# Revit family: Haworth_Masters_Desk_DoublePedRectangularTop
name_source: partatom
category: Furniture Systems
revit_build: Autodesk Revit 2018 (Build: 20170223_1515(x64)
units: mm (PartAtom-declared; Revit-internal decimal feet)

## family parameters
Always vertical = Yes
Cut with Voids When Loaded = No
OmniClass Number = 23.40.70.14.64.21
OmniClass Title = Systems Furniture
Part Type = Normal
Room Calculation Point = No
Round Connector Dimension = Use Diameter
Shared = No
Work Plane-Based = No

## types (4) — shared parameters
Actual Depth = 36"
Actual Height = 29 1/8"
Actual Width = 78"
Assembly Code = E2020200
Bar Pull = No
Classic Pull = Yes
Custom Size = No
Depth = 36"
Finger Pull = No
Linear Pull = No
Manufacturer = Haworth
Max. Depth = 36"
Max. Width = 78"
Min. Depth = 30"
Min. Width = 66"
Model = Haworth Masters
Pedestal Depth = 29"
Revision Number = 1
Size = Verify Final Dim. w/ Haworth
Standard Depths = 30, 36 in.
Standard Widths = 66, 72, 78 in.
Sustainability Info = https://www.haworth.com
Thickness = 1 3/16"
URL = www.haworth.com
URL - Product = http://www.haworth.com
Warranty = http://www.haworth.com
Width = 78"

## per-type parameters (varying)
| type | Description | Full Overlay Modesty | Inset Modesty | Void Dimension |
| False Pedestal Modesty - Two Box/Box/File - 36d 78w | Haworth - Masters Desk - Double Ped - Rectangular Top - False Pedestal Modesty - Two Box/Box/File - 36d 78w | No | Yes | 0" |
| False Pedestal Modesty - One Box/Box/File & One File/File - 36d 78w | Haworth - Masters Desk - Double Ped - Rectangular Top - False Pedestal Modesty - One Box/Box/File and One File/File - 36d 78w | No | Yes | 0" |
| Full Overlay Modesty - Two Box/Box/File - 36d 78w | Haworth - Masters Desk - Double Ped - Rectangular Top - Full Overlay Modesty - Two Box/Box/File - 36d 78w | Yes | No | 1" |
| Full Overlay Modesty - One Box/Box/File & One File/File - 36d 78w | Haworth - Masters Desk - Double Ped - Rectangular Top - Full Overlay Modesty - One Box/Box/File and One File/File - 36d 78w | Yes | No | 1" |

## geometry (parser evidence)
native form markers: Sweep x12
no freeform markers — native parametric forms only
